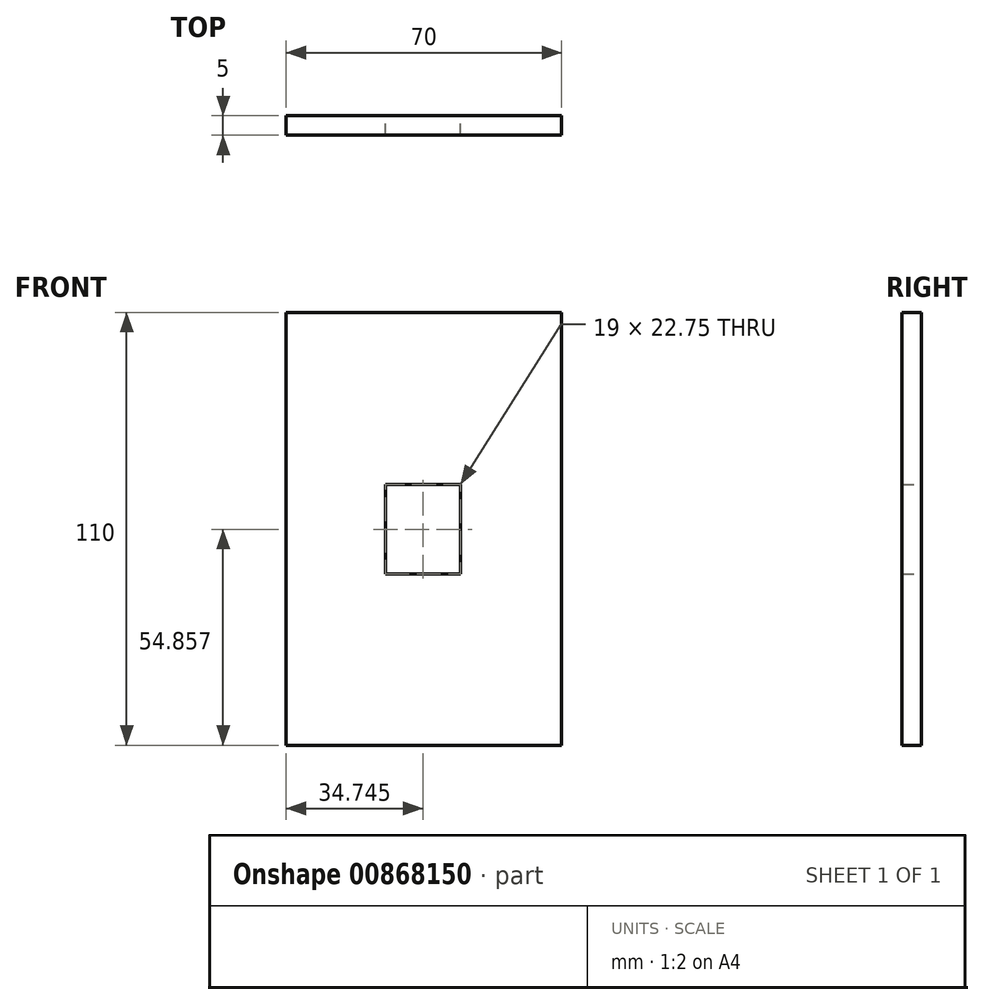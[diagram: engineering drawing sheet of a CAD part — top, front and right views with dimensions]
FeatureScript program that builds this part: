
annotation { "Feature Type Name" : "Feature", "Feature Type Description" : "" }
export const myFeature = defineFeature(function(context is Context, id is Id, definition is map)
    precondition{}
    {
        {
            var Q0;
            Q0=qCreatedBy(makeId("Front.planeOp"),FACE);
            var sketch = newSketch(context, id + "F0", { "sketchPlane" : qUnion([Q0])});
            skLineSegment(sketch, "E0.bottom", {"start": v(-34.62, 55.4) * mm, "end": v(35.38, 55.4) * mm});
            skLineSegment(sketch, "E0.top", {"start": v(-34.62, -54.6) * mm, "end": v(35.38, -54.6) * mm});
            skLineSegment(sketch, "E0.left", {"start": v(-34.62, 55.4) * mm, "end": v(-34.62, -54.6) * mm});
            skLineSegment(sketch, "E0.right", {"start": v(35.38, 55.4) * mm, "end": v(35.38, -54.6) * mm});
            skLineSegment(sketch, "E1.bottom", {"start": v(-9.38, 11.62) * mm, "end": v(9.63, 11.62) * mm});
            skLineSegment(sketch, "E1.top", {"start": v(-9.38, -11.13) * mm, "end": v(9.63, -11.13) * mm});
            skLineSegment(sketch, "E1.left", {"start": v(-9.38, 11.62) * mm, "end": v(-9.38, -11.13) * mm});
            skLineSegment(sketch, "E1.right", {"start": v(9.63, 11.62) * mm, "end": v(9.63, -11.13) * mm});
            skSolve(sketch);
        }
        {
            var Q0;
            Q0 = qSketchRegion(id + "F0", true);
            extrude(context, id + "F1", {"entities" : qUnion([Q0]), "depth" : 5 * mm, "offsetDistance" : 25 * mm});
        }
        {
            var Q0;
            Q0 = qSketchRegion(id + "F0", true);
            extrude(context, id + "F2", {"entities" : qUnion([Q0]), "operationType" : NewBodyOperationType.ADD, "depth" : 5 * mm, "offsetDistance" : 25 * mm});
        }
    });
